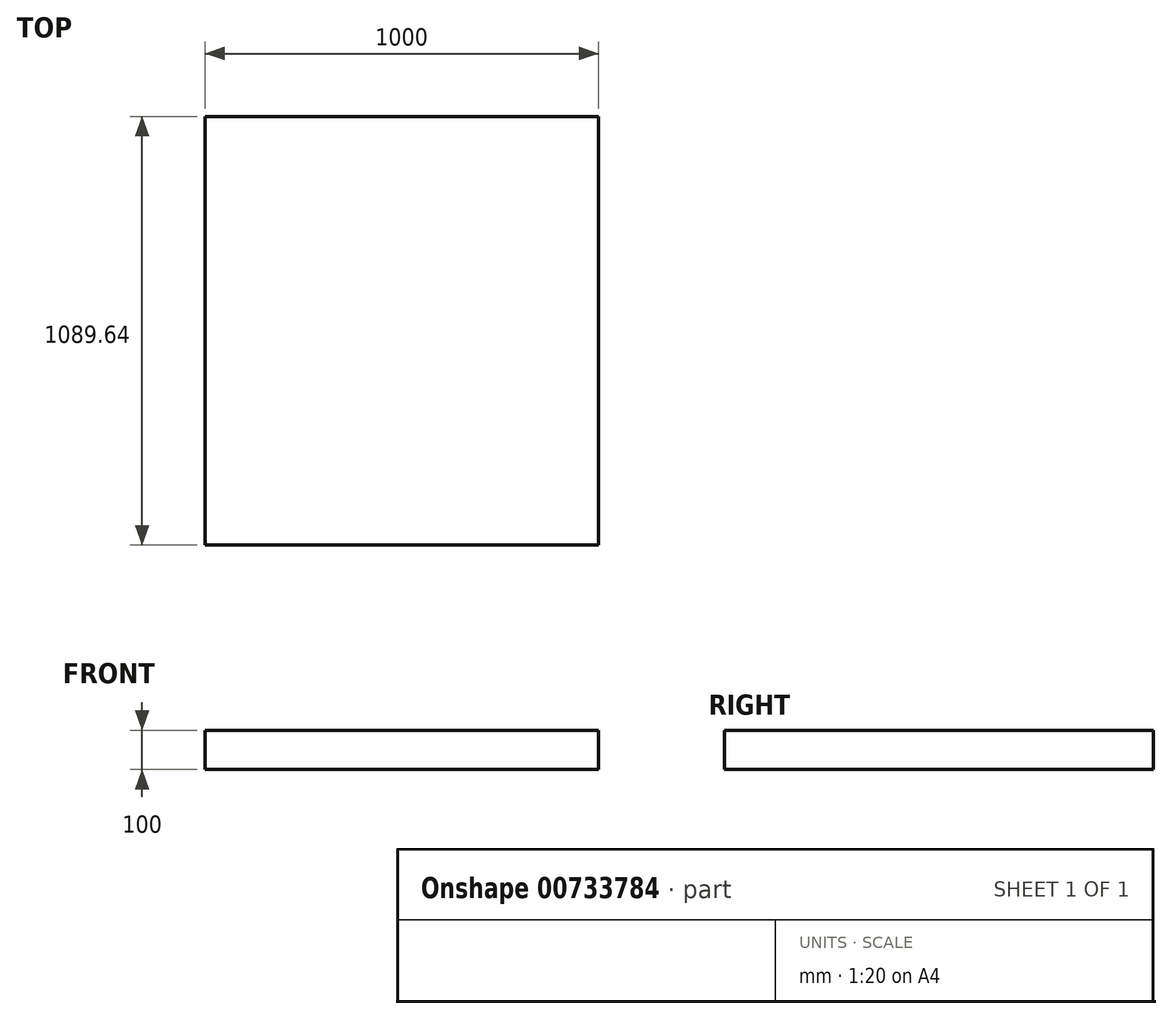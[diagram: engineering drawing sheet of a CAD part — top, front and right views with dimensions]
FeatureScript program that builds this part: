
annotation { "Feature Type Name" : "Feature", "Feature Type Description" : "" }
export const myFeature = defineFeature(function(context is Context, id is Id, definition is map)
    precondition{}
    {
        {
            var Q0;
            Q0=qCreatedBy(makeId("Top.planeOp"),FACE);
            var sketch = newSketch(context, id + "F0", { "sketchPlane" : qUnion([Q0])});
            skLineSegment(sketch, "E0", {"start": v(0, 0) * mm, "end": v(0, 10000) * mm, "construction": true});
            skLineSegment(sketch, "E1", {"start": v(0, 10000) * mm, "end": v(5000, 10000) * mm, "construction": true});
            skLineSegment(sketch, "E2", {"start": v(0, 10000) * mm, "end": v(-5000, 10000) * mm, "construction": true});
            skLineSegment(sketch, "E3", {"start": v(0, 0) * mm, "end": v(-5000, 0) * mm, "construction": true});
            skLineSegment(sketch, "E4", {"start": v(0, 0) * mm, "end": v(5000, 0) * mm, "construction": true});
            skLineSegment(sketch, "E5", {"start": v(5000, 0) * mm, "end": v(5000, -2000) * mm});
            skLineSegment(sketch, "E6", {"start": v(5000, 0) * mm, "end": v(5000, 2000) * mm});
            skLineSegment(sketch, "E7.bottom", {"start": v(0, 0) * mm, "end": v(1000, 0) * mm});
            skLineSegment(sketch, "E7.top", {"start": v(0, -1089.64) * mm, "end": v(1000, -1089.64) * mm});
            skLineSegment(sketch, "E7.left", {"start": v(0, 0) * mm, "end": v(0, -1089.64) * mm});
            skLineSegment(sketch, "E7.right", {"start": v(1000, 0) * mm, "end": v(1000, -1089.64) * mm});
            skSolve(sketch);
        }
        {
            var Q0;
            Q0=qSketchRegion(id+"F0",true);
            extrude(context, id + "F1", {"entities" : qUnion([Q0]), "oppositeDirection" : true, "depth" : 100 * mm, "offsetDistance" : 25 * mm});
        }
    });
